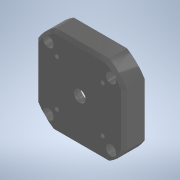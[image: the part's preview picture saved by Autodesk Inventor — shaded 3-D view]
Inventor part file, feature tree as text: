
AUTODESK INVENTOR PART (.ipt)
format: ipt  version: 2022 (Build 260153000, 153)  size: 183,296 bytes
history: mixed  units: in
note: dims shown in document units (in); Inventor stores cm internally (conversion verified against a paired STEP export)
features: extrude x1, sketch x1, chamfer x1, imported_body x1
ambient origin geometry x8: Origin, YZ Plane, XZ Plane, XY Plane, X Axis, Y Axis, Z Axis, Center Point
bodies: Solid1 (imported_parasolid)
feature tree (4):
  extrude  "Extrusion1"  Depth=0.3937in TaperAngle=0.0deg
  sketch  "Sketch1"  dims[d0=0.1102in d1=0.3937in d2=0.0in]
  chamfer  "Chamfer2"  [1 undecoded]
  imported_body  NMx_Import_Brep_tag  [imported B-rep: ~38 faces, bbox_mm=[58.0, 60.0, 14.0]]
note: 1 required parameter value undecoded (feature->parameter linkage not recoverable at this tier; creation-order binding heuristic only, values carry confidence <= 0.55)
